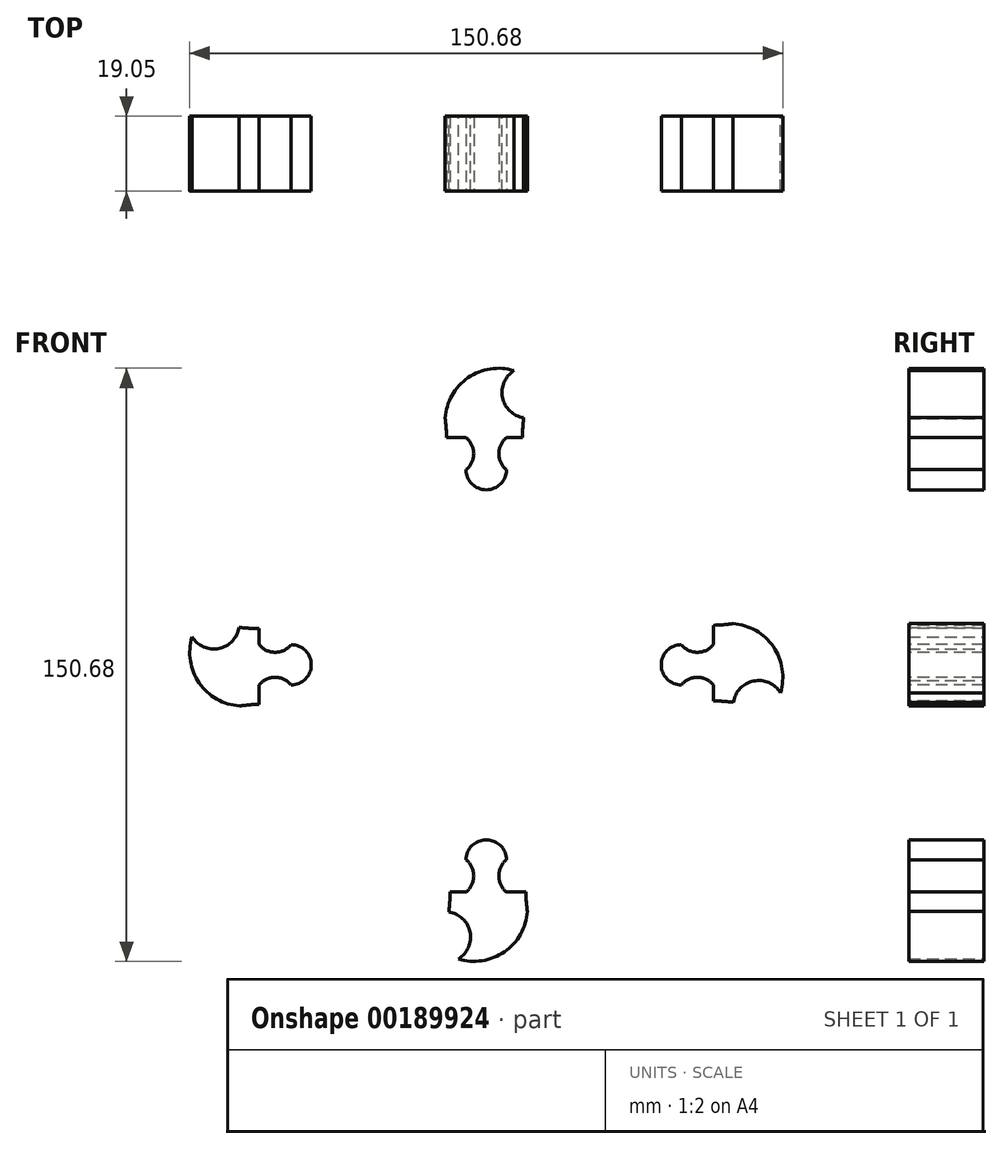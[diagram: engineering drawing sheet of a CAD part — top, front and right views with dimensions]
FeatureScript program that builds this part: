
annotation { "Feature Type Name" : "Feature", "Feature Type Description" : "" }
export const myFeature = defineFeature(function(context is Context, id is Id, definition is map)
    precondition{}
    {
        {
            var Q0;
            Q0=qCreatedBy(makeId("Front.planeOp"),FACE);
            var sketch = newSketch(context, id + "F0", { "sketchPlane" : qUnion([Q0])});
            skArc(sketch, "E0", {"start": v(-10.45, 62.63) * mm, "mid": v(0.47, -63.5) * mm, "end": v(9.52, 62.78) * mm});
            skArc(sketch, "E1", {"start": v(7.09, 74.74) * mm, "mid": v(-4.61, 72.94) * mm, "end": v(-10.45, 62.63) * mm});
            skArc(sketch, "E2", {"start": v(7.09, 74.74) * mm, "mid": v(4.13, 67.91) * mm, "end": v(9.52, 62.78) * mm});
            skArc(sketch, "E3.1.0", {"start": v(-74.74, 7.09) * mm, "mid": v(-72.94, -4.61) * mm, "end": v(-62.63, -10.45) * mm});
            skArc(sketch, "E3.1.1", {"start": v(-74.74, 7.09) * mm, "mid": v(-67.91, 4.13) * mm, "end": v(-62.78, 9.52) * mm});
            skArc(sketch, "E3.2.0", {"start": v(-7.09, -74.74) * mm, "mid": v(4.61, -72.94) * mm, "end": v(10.45, -62.63) * mm});
            skArc(sketch, "E3.2.1", {"start": v(-7.09, -74.74) * mm, "mid": v(-4.13, -67.91) * mm, "end": v(-9.52, -62.78) * mm});
            skArc(sketch, "E3.3.0", {"start": v(74.74, -7.09) * mm, "mid": v(72.94, 4.61) * mm, "end": v(62.63, 10.45) * mm});
            skArc(sketch, "E3.3.1", {"start": v(74.74, -7.09) * mm, "mid": v(67.91, -4.13) * mm, "end": v(62.78, -9.52) * mm});
            skSolve(sketch);
        }
        {
            var Q0;
            {var subQ6=sQuery(id+"F0.wireOp",EDGE,"E1");Q0=makeQuery(id+"F0.imprint","IMPRINT",FACE,{"disambiguationData":[TD([[makeQuery(id+"F0.imprint","IMPRINT",EDGE,{"derivedFrom":subQ6}),1.0]])]});}
            var Q1;
            {var subQ0=sQuery(id+"F0.wireOp",EDGE,"E3.1.0");Q1=makeQuery(id+"F0.imprint","IMPRINT",FACE,{"disambiguationData":[TD([[makeQuery(id+"F0.imprint","IMPRINT",EDGE,{"derivedFrom":subQ0}),1.0]])]});}
            var Q2;
            {var subQ0=sQuery(id+"F0.wireOp",EDGE,"E3.3.0");Q2=makeQuery(id+"F0.imprint","IMPRINT",FACE,{"disambiguationData":[TD([[makeQuery(id+"F0.imprint","IMPRINT",EDGE,{"derivedFrom":subQ0}),1.0]])]});}
            var Q3;
            {var subQ0=sQuery(id+"F0.wireOp",EDGE,"E3.2.0");Q3=makeQuery(id+"F0.imprint","IMPRINT",FACE,{"disambiguationData":[TD([[makeQuery(id+"F0.imprint","IMPRINT",EDGE,{"derivedFrom":subQ0}),1.0]])]});}
            extrude(context, id + "F1", {"entities" : qUnion([Q0, Q1, Q2, Q3]), "depth" : 19.05 * mm});
        }
        {
            var Q0;
            Q0=makeQuery(id+"F1.opExtrude","CAP_FACE",FACE,{"disambiguationData":[OSD([sQuery(id+"F0.wireOp",EDGE,"E0"),sQuery(id+"F0.wireOp",EDGE,"E1"),sQuery(id+"F0.wireOp",EDGE,"E2"),sQuery(id+"F0.wireOp",EDGE,"E3.1.0"),sQuery(id+"F0.wireOp",EDGE,"E3.1.1"),sQuery(id+"F0.wireOp",EDGE,"E3.2.0"),sQuery(id+"F0.wireOp",EDGE,"E3.2.1"),sQuery(id+"F0.wireOp",EDGE,"E3.3.0"),sQuery(id+"F0.wireOp",EDGE,"E3.3.1")])],"isStart":true});
            var sketch = newSketch(context, id + "F2", { "sketchPlane" : qUnion([Q0])});
            skPoint(sketch, "E4.middle", {"position": v(0, 0) * mm});
            skPoint(sketch, "E4.top.end.orphan", {"position": v(1.59, -1.59) * mm});
            skPoint(sketch, "E4.left.end.orphan", {"position": v(-1.59, -1.59) * mm});
            skPoint(sketch, "E4.bottom.end.orphan", {"position": v(1.59, 1.59) * mm});
            skPoint(sketch, "E4.bottom.start.orphan", {"position": v(-1.59, 1.59) * mm});
            skArc(sketch, "E5", {"start": v(-2.6, 1.59) * mm, "mid": v(0, -3.05) * mm, "end": v(2.6, 1.59) * mm});
            skLineSegment(sketch, "E6", {"start": v(2.6, 1.59) * mm, "end": v(-1.59, 1.59) * mm});
            skLineSegment(sketch, "E7", {"start": v(-1.59, 1.59) * mm, "end": v(-2.6, 1.59) * mm});
            skSolve(sketch);
        }
        {
            var Q0;
            Q0=makeQuery(id+"F1.opExtrude","CAP_FACE",FACE,{"disambiguationData":[OSD([sQuery(id+"F0.wireOp",EDGE,"E0"),sQuery(id+"F0.wireOp",EDGE,"E1"),sQuery(id+"F0.wireOp",EDGE,"E2"),sQuery(id+"F0.wireOp",EDGE,"E3.1.0"),sQuery(id+"F0.wireOp",EDGE,"E3.1.1"),sQuery(id+"F0.wireOp",EDGE,"E3.2.0"),sQuery(id+"F0.wireOp",EDGE,"E3.2.1"),sQuery(id+"F0.wireOp",EDGE,"E3.3.0"),sQuery(id+"F0.wireOp",EDGE,"E3.3.1")])],"isStart":false});
            var sketch = newSketch(context, id + "F3", { "sketchPlane" : qUnion([Q0])});
            skArc(sketch, "E8", {"start": v(9.52, 62.78) * mm, "mid": v(23.24, 23.59) * mm, "end": v(62.63, 10.45) * mm});
            skLineSegment(sketch, "E9", {"start": v(9.52, 62.78) * mm, "end": v(39.87, 79.15) * mm});
            skLineSegment(sketch, "E10", {"start": v(39.87, 79.15) * mm, "end": v(86.09, 35.23) * mm});
            skLineSegment(sketch, "E11", {"start": v(86.09, 35.23) * mm, "end": v(62.63, 10.45) * mm});
            skPoint(sketch, "E12.center", {"position": v(0, 0) * mm});
            skLineSegment(sketch, "E13.1.0", {"start": v(-62.78, 9.52) * mm, "end": v(-79.15, 39.87) * mm});
            skLineSegment(sketch, "E13.1.1", {"start": v(-79.15, 39.87) * mm, "end": v(-35.23, 86.09) * mm});
            skLineSegment(sketch, "E13.1.2", {"start": v(-35.23, 86.09) * mm, "end": v(-10.45, 62.63) * mm});
            skArc(sketch, "E13.1.3", {"start": v(-62.78, 9.52) * mm, "mid": v(-23.59, 23.24) * mm, "end": v(-10.45, 62.63) * mm});
            skLineSegment(sketch, "E13.2.0", {"start": v(-9.52, -62.78) * mm, "end": v(-39.87, -79.15) * mm});
            skLineSegment(sketch, "E13.2.1", {"start": v(-39.87, -79.15) * mm, "end": v(-86.09, -35.23) * mm});
            skLineSegment(sketch, "E13.2.2", {"start": v(-86.09, -35.23) * mm, "end": v(-62.63, -10.45) * mm});
            skArc(sketch, "E13.2.3", {"start": v(-9.52, -62.78) * mm, "mid": v(-23.24, -23.59) * mm, "end": v(-62.63, -10.45) * mm});
            skLineSegment(sketch, "E13.3.0", {"start": v(62.78, -9.52) * mm, "end": v(79.15, -39.87) * mm});
            skLineSegment(sketch, "E13.3.1", {"start": v(79.15, -39.87) * mm, "end": v(35.23, -86.09) * mm});
            skLineSegment(sketch, "E13.3.2", {"start": v(35.23, -86.09) * mm, "end": v(10.45, -62.63) * mm});
            skArc(sketch, "E13.3.3", {"start": v(62.78, -9.52) * mm, "mid": v(23.59, -23.24) * mm, "end": v(10.45, -62.63) * mm});
            skSolve(sketch);
        }
        {
            var Q0;
            Q0 = qSketchRegion(id + "F3", true);
            extrude(context, id + "F4", {"entities" : qUnion([Q0]), "operationType" : NewBodyOperationType.REMOVE, "endBound" : BoundingType.THROUGH_ALL, "oppositeDirection" : true, "depth" : 25.4 * mm});
        }
        {
            var Q0;
            Q0=makeQuery(id+"F1.opExtrude","CAP_FACE",FACE,{"disambiguationData":[OSD([sQuery(id+"F0.wireOp",EDGE,"E0"),sQuery(id+"F0.wireOp",EDGE,"E1"),sQuery(id+"F0.wireOp",EDGE,"E2"),sQuery(id+"F0.wireOp",EDGE,"E3.1.0"),sQuery(id+"F0.wireOp",EDGE,"E3.1.1"),sQuery(id+"F0.wireOp",EDGE,"E3.2.0"),sQuery(id+"F0.wireOp",EDGE,"E3.2.1"),sQuery(id+"F0.wireOp",EDGE,"E3.3.0"),sQuery(id+"F0.wireOp",EDGE,"E3.3.1")])],"isStart":false});
            var sketch = newSketch(context, id + "F5", { "sketchPlane" : qUnion([Q0])});
            skArc(sketch, "E14", {"start": v(5.12, 49.56) * mm, "mid": v(0, 44.46) * mm, "end": v(-5.12, 49.56) * mm});
            skLineSegment(sketch, "E15", {"start": v(0, 49.58) * mm, "end": v(0, 74.98) * mm, "construction": true});
            skArc(sketch, "E16", {"start": v(-5.12, 49.56) * mm, "mid": v(-3.17, 53.64) * mm, "end": v(-5.12, 57.71) * mm});
            skArc(sketch, "E17.MirrorCS", {"start": v(5.12, 49.56) * mm, "mid": v(3.18, 53.64) * mm, "end": v(5.12, 57.71) * mm});
            skLineSegment(sketch, "E18", {"start": v(-5.12, 57.71) * mm, "end": v(-10.04, 57.71) * mm});
            skLineSegment(sketch, "E19", {"start": v(5.12, 57.71) * mm, "end": v(9.19, 57.71) * mm});
            skArc(sketch, "E20", {"start": v(7.09, 74.74) * mm, "mid": v(-7.5, 76.43) * mm, "end": v(-13.71, 63.11) * mm});
            skArc(sketch, "E21", {"start": v(7.09, 74.74) * mm, "mid": v(4.19, 67.92) * mm, "end": v(9.52, 62.78) * mm});
            skArc(sketch, "E22.1.0", {"start": v(-49.56, 5.12) * mm, "mid": v(-53.64, 3.18) * mm, "end": v(-57.71, 5.12) * mm});
            skArc(sketch, "E22.1.1", {"start": v(-49.56, 5.12) * mm, "mid": v(-44.46, 0) * mm, "end": v(-49.56, -5.12) * mm});
            skLineSegment(sketch, "E22.1.2", {"start": v(-49.58, 0) * mm, "end": v(-74.98, 0) * mm, "construction": true});
            skArc(sketch, "E22.1.3", {"start": v(-74.74, 7.09) * mm, "mid": v(-76.43, -7.5) * mm, "end": v(-63.11, -13.71) * mm});
            skArc(sketch, "E22.1.4", {"start": v(-49.56, -5.12) * mm, "mid": v(-53.64, -3.17) * mm, "end": v(-57.71, -5.12) * mm});
            skArc(sketch, "E22.1.5", {"start": v(-74.74, 7.09) * mm, "mid": v(-67.92, 4.19) * mm, "end": v(-62.78, 9.52) * mm});
            skArc(sketch, "E22.1.6", {"start": v(-49.56, 5.12) * mm, "mid": v(-53.64, 3.18) * mm, "end": v(-57.71, 5.12) * mm});
            skLineSegment(sketch, "E22.1.7", {"start": v(-57.71, -5.12) * mm, "end": v(-57.71, -10.04) * mm});
            skLineSegment(sketch, "E22.1.8", {"start": v(-57.71, 5.12) * mm, "end": v(-57.71, 9.19) * mm});
            skArc(sketch, "E22.2.0", {"start": v(-5.12, -49.56) * mm, "mid": v(-3.18, -53.64) * mm, "end": v(-5.12, -57.71) * mm});
            skArc(sketch, "E22.2.1", {"start": v(-5.12, -49.56) * mm, "mid": v(0, -44.46) * mm, "end": v(5.12, -49.56) * mm});
            skLineSegment(sketch, "E22.2.2", {"start": v(0, -49.58) * mm, "end": v(0, -74.98) * mm, "construction": true});
            skArc(sketch, "E22.2.3", {"start": v(-7.09, -74.74) * mm, "mid": v(7.5, -76.43) * mm, "end": v(13.71, -63.11) * mm});
            skArc(sketch, "E22.2.4", {"start": v(5.12, -49.56) * mm, "mid": v(3.17, -53.64) * mm, "end": v(5.12, -57.71) * mm});
            skArc(sketch, "E22.2.5", {"start": v(-7.09, -74.74) * mm, "mid": v(-4.19, -67.92) * mm, "end": v(-9.52, -62.78) * mm});
            skArc(sketch, "E22.2.6", {"start": v(-5.12, -49.56) * mm, "mid": v(-3.18, -53.64) * mm, "end": v(-5.12, -57.71) * mm});
            skLineSegment(sketch, "E22.2.7", {"start": v(5.12, -57.71) * mm, "end": v(10.04, -57.71) * mm});
            skLineSegment(sketch, "E22.2.8", {"start": v(-5.12, -57.71) * mm, "end": v(-9.19, -57.71) * mm});
            skArc(sketch, "E22.3.0", {"start": v(49.56, -5.12) * mm, "mid": v(53.64, -3.18) * mm, "end": v(57.71, -5.12) * mm});
            skArc(sketch, "E22.3.1", {"start": v(49.56, -5.12) * mm, "mid": v(44.46, 0) * mm, "end": v(49.56, 5.12) * mm});
            skLineSegment(sketch, "E22.3.2", {"start": v(49.58, 0) * mm, "end": v(74.98, 0) * mm, "construction": true});
            skArc(sketch, "E22.3.3", {"start": v(74.74, -7.09) * mm, "mid": v(76.43, 7.5) * mm, "end": v(63.11, 13.71) * mm});
            skArc(sketch, "E22.3.4", {"start": v(49.56, 5.12) * mm, "mid": v(53.64, 3.17) * mm, "end": v(57.71, 5.12) * mm});
            skArc(sketch, "E22.3.5", {"start": v(74.74, -7.09) * mm, "mid": v(67.92, -4.19) * mm, "end": v(62.78, -9.52) * mm});
            skArc(sketch, "E22.3.6", {"start": v(49.56, -5.12) * mm, "mid": v(53.64, -3.18) * mm, "end": v(57.71, -5.12) * mm});
            skLineSegment(sketch, "E22.3.7", {"start": v(57.71, 5.12) * mm, "end": v(57.71, 10.04) * mm});
            skLineSegment(sketch, "E22.3.8", {"start": v(57.71, -5.12) * mm, "end": v(57.71, -9.19) * mm});
            skPoint(sketch, "E22.center", {"position": v(0, 0) * mm});
            skLineSegment(sketch, "E23", {"start": v(-10.04, 57.71) * mm, "end": v(-11.15, 60.78) * mm});
            skLineSegment(sketch, "E24", {"start": v(-11.15, 60.78) * mm, "end": v(-13.71, 63.11) * mm});
            skLineSegment(sketch, "E25", {"start": v(9.19, 57.71) * mm, "end": v(11.23, 57.3) * mm});
            skLineSegment(sketch, "E26", {"start": v(11.23, 57.3) * mm, "end": v(9.52, 62.78) * mm});
            skLineSegment(sketch, "E27.1.0", {"start": v(-60.78, -11.15) * mm, "end": v(-63.11, -13.71) * mm});
            skLineSegment(sketch, "E27.1.1", {"start": v(-57.71, -10.04) * mm, "end": v(-60.78, -11.15) * mm});
            skLineSegment(sketch, "E27.1.2", {"start": v(-57.3, 11.23) * mm, "end": v(-62.78, 9.52) * mm});
            skLineSegment(sketch, "E27.1.3", {"start": v(-57.71, 9.19) * mm, "end": v(-57.3, 11.23) * mm});
            skLineSegment(sketch, "E27.2.0", {"start": v(11.15, -60.78) * mm, "end": v(13.71, -63.11) * mm});
            skLineSegment(sketch, "E27.2.1", {"start": v(10.04, -57.71) * mm, "end": v(11.15, -60.78) * mm});
            skLineSegment(sketch, "E27.2.2", {"start": v(-11.23, -57.3) * mm, "end": v(-9.52, -62.78) * mm});
            skLineSegment(sketch, "E27.2.3", {"start": v(-9.19, -57.71) * mm, "end": v(-11.23, -57.3) * mm});
            skLineSegment(sketch, "E27.3.0", {"start": v(60.78, 11.15) * mm, "end": v(63.11, 13.71) * mm});
            skLineSegment(sketch, "E27.3.1", {"start": v(57.71, 10.04) * mm, "end": v(60.78, 11.15) * mm});
            skLineSegment(sketch, "E27.3.2", {"start": v(57.3, -11.23) * mm, "end": v(62.78, -9.52) * mm});
            skLineSegment(sketch, "E27.3.3", {"start": v(57.71, -9.19) * mm, "end": v(57.3, -11.23) * mm});
            skSolve(sketch);
        }
        {
            var Q0;
            Q0=makeQuery(id+"F5.imprint","IMPRINT",FACE,{"disambiguationData":[TD([[makeQuery(id+"F5.imprint","IMPRINT",EDGE,{"derivedFrom":sQuery(id+"F5.wireOp",EDGE,"E14")}),-1.0]])]});
            var Q1;
            Q1=makeQuery(id+"F5.imprint","IMPRINT",FACE,{"disambiguationData":[TD([[makeQuery(id+"F5.imprint","IMPRINT",EDGE,{"derivedFrom":sQuery(id+"F5.wireOp",EDGE,"E22.1.1")}),-1.0]])]});
            var Q2;
            Q2=makeQuery(id+"F5.imprint","IMPRINT",FACE,{"disambiguationData":[TD([[makeQuery(id+"F5.imprint","IMPRINT",EDGE,{"derivedFrom":sQuery(id+"F5.wireOp",EDGE,"E22.2.1")}),-1.0]])]});
            var Q3;
            Q3=makeQuery(id+"F5.imprint","IMPRINT",FACE,{"disambiguationData":[TD([[makeQuery(id+"F5.imprint","IMPRINT",EDGE,{"derivedFrom":sQuery(id+"F5.wireOp",EDGE,"E22.3.1")}),-1.0]])]});
            extrude(context, id + "F6", {"entities" : qUnion([Q0, Q1, Q2, Q3]), "operationType" : NewBodyOperationType.REMOVE, "endBound" : BoundingType.THROUGH_ALL, "oppositeDirection" : true, "depth" : 25.4 * mm});
        }
        {
            var Q0;
            Q0 = qSketchRegion(id + "F2", true);
            extrude(context, id + "F7", {"entities" : qUnion([Q0]), "operationType" : NewBodyOperationType.REMOVE, "endBound" : BoundingType.THROUGH_ALL, "oppositeDirection" : true, "depth" : 25.4 * mm});
        }
    });
